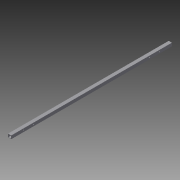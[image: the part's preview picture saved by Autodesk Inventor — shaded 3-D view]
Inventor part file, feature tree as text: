
AUTODESK INVENTOR PART (.ipt)
format: ipt  version: 2016 (Build 200138000, 138)  size: 134,144 bytes
history: native  units: in
note: dims shown in document units (in); Inventor stores cm internally (conversion verified against a paired STEP export)
features: reference x8, sketch x6, hole x4, extrude x1
ambient origin geometry x8: Origin, YZ Plane, XZ Plane, XY Plane, X Axis, Y Axis, Z Axis, Center Point
bodies: Solid1 (feature_tree)
feature tree (19):
  extrude  "Extrusion1"  Depth=1.0in
  hole  "Hole1"  [1 undecoded]
  sketch  "Sketch3"  dims[d5=0.266in d6=0.75in d7=0.375in d8=0.25in d9=0.5635in d10=0.5in d11=0.8108in]
  hole  "Hole2"  [1 undecoded]
  hole  "Hole3"  [1 undecoded]
  hole  "Hole4"  [1 undecoded]
  sketch  "Sketch1"  dims[d0=1.0in d1=1.0in]
  sketch  "Sketch2"  dims[d2=0.12in d3=50.0in d4=0.0in]
  reference  "Reference1"
  reference  "Reference2"
  reference  "Reference3"
  reference  "Reference4"
  sketch  "Sketch5"  dims[d12=0.5in d13=0.75in d14=0.375in d15=0.25in d16=0.5635in d17=0.125in d18=0.8108in d19=4.75in]
  sketch  "Sketch6"  dims[d20=4.5in d21=4.75in]
  sketch  "Sketch7"  dims[d22=4.5in d23=0.2656in d24=0.75in d25=0.375in d26=0.25in d27=0.5635in d28=0.125in d29=0.8108in d31=0.5in d32=0.75in d33=0.375in d34=0.25in d35=0.5635in d36=0.125in d37=0.8108in]
  reference  "Reference5"
  reference  "Reference6"
  reference  "Reference7"
  reference  "Reference8"
note: 4 required parameter values undecoded (feature->parameter linkage not recoverable at this tier; creation-order binding heuristic only, values carry confidence <= 0.55)
